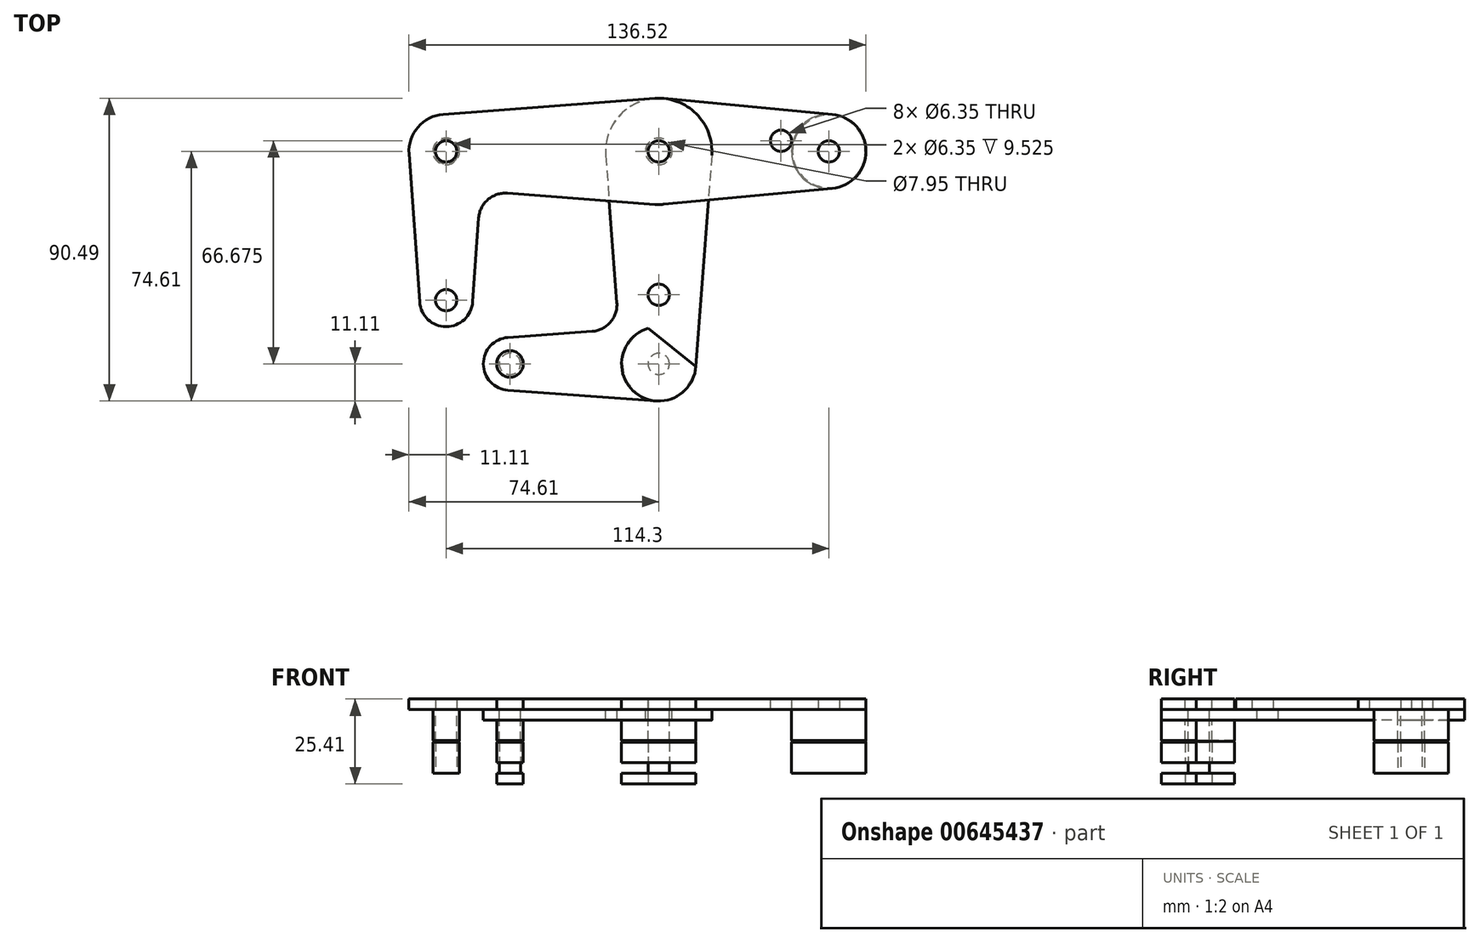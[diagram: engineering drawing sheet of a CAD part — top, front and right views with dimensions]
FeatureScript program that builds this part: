
annotation { "Feature Type Name" : "Feature", "Feature Type Description" : "" }
export const myFeature = defineFeature(function(context is Context, id is Id, definition is map)
    precondition{}
    {
        {
            var Q0;
            Q0=qCreatedBy(makeId("Top.planeOp"),FACE);
            var sketch = newSketch(context, id + "F0", { "sketchPlane" : qUnion([Q0])});
            skCircle(sketch, "E0", {"center": v(0, 0) * mm, "radius": 15.88 * mm});
            skCircle(sketch, "E1", {"center": v(0, 0) * mm, "radius": 3.98 * mm});
            skCircle(sketch, "E2", {"center": v(-63.5, 0) * mm, "radius": 11.11 * mm});
            skCircle(sketch, "E3", {"center": v(50.8, 0) * mm, "radius": 11.11 * mm});
            skCircle(sketch, "E4", {"center": v(-63.5, -44.45) * mm, "radius": 7.94 * mm});
            skCircle(sketch, "E5", {"center": v(50.8, 0) * mm, "radius": 3.18 * mm});
            skCircle(sketch, "E6", {"center": v(36.53, 3.18) * mm, "radius": 3.18 * mm});
            skCircle(sketch, "E7", {"center": v(-63.5, -44.45) * mm, "radius": 3.18 * mm});
            skCircle(sketch, "E8", {"center": v(-63.5, 0) * mm, "radius": 3.18 * mm});
            skLineSegment(sketch, "E9", {"start": v(-71.42, -45.02) * mm, "end": v(-74.58, -0.8) * mm});
            skLineSegment(sketch, "E10", {"start": v(-64.33, 11.08) * mm, "end": v(-1.2, 15.83) * mm});
            skLineSegment(sketch, "E11", {"start": v(1.49, 15.8) * mm, "end": v(51.84, 11.06) * mm});
            skLineSegment(sketch, "E12.MirrorCS", {"start": v(1.49, -15.8) * mm, "end": v(51.84, -11.06) * mm});
            skLineSegment(sketch, "E13.MirrorCS", {"start": v(-45.26, -12.52) * mm, "end": v(-1.2, -15.83) * mm});
            skLineSegment(sketch, "E14", {"start": v(-63.5, 0) * mm, "end": v(-63.5, -44.45) * mm, "construction": true});
            skLineSegment(sketch, "E15.MirrorCS", {"start": v(-55.58, -45.02) * mm, "end": v(-53.78, -19.88) * mm});
            skPoint(sketch, "E16.newPointA", {"position": v(-64.33, -11.08) * mm});
            skPoint(sketch, "E16.newPointB", {"position": v(-52.42, -0.8) * mm});
            skArc(sketch, "E16.filletArc", {"start": v(-45.26, -12.52) * mm, "mid": v(-51.05, -14.43) * mm, "end": v(-53.78, -19.88) * mm});
            skCircle(sketch, "E17", {"center": v(0, 0) * mm, "radius": 3.18 * mm});
            skCircle(sketch, "E18", {"center": v(0, -63.5) * mm, "radius": 11.11 * mm});
            skCircle(sketch, "E19", {"center": v(0, -42.85) * mm, "radius": 3.18 * mm});
            skCircle(sketch, "E20", {"center": v(-44.45, -63.5) * mm, "radius": 7.94 * mm});
            skCircle(sketch, "E21", {"center": v(-44.45, -63.5) * mm, "radius": 3.18 * mm});
            skCircle(sketch, "E22", {"center": v(0, -63.5) * mm, "radius": 3.18 * mm});
            skLineSegment(sketch, "E23", {"start": v(15.83, -1.2) * mm, "end": v(11.08, -64.33) * mm});
            skLineSegment(sketch, "E24", {"start": v(-15.83, -1.2) * mm, "end": v(-12.52, -45.26) * mm});
            skLineSegment(sketch, "E25", {"start": v(-45.02, -71.42) * mm, "end": v(-0.8, -74.58) * mm});
            skLineSegment(sketch, "E26", {"start": v(-45.02, -55.58) * mm, "end": v(-19.88, -53.78) * mm});
            skArc(sketch, "E27.filletArc", {"start": v(-19.88, -53.78) * mm, "mid": v(-14.43, -51.05) * mm, "end": v(-12.52, -45.26) * mm});
            skLineSegment(sketch, "E28", {"start": v(0, -63.5) * mm, "end": v(0, 0) * mm, "construction": true});
            skLineSegment(sketch, "E29", {"start": v(-44.45, -63.5) * mm, "end": v(0, -63.5) * mm, "construction": true});
            skLineSegment(sketch, "E30", {"start": v(0, 0) * mm, "end": v(50.8, 0) * mm, "construction": true});
            skLineSegment(sketch, "E31", {"start": v(-63.5, 0) * mm, "end": v(0, 0) * mm, "construction": true});
            skSolve(sketch);
        }
        {
            var Q0;
            {var subQ0=sQuery(id+"F0.wireOp",EDGE,"E9");Q0=makeQuery(id+"F0.imprint","IMPRINT",FACE,{"disambiguationData":[TD([[makeQuery(id+"F0.imprint","IMPRINT",EDGE,{"derivedFrom":subQ0}),-1.0]])]});}
            var Q1;
            Q1=makeQuery(id+"F0.imprint","IMPRINT",FACE,{"disambiguationData":[TD([[makeQuery(id+"F0.imprint","IMPRINT",EDGE,{"derivedFrom":sQuery(id+"F0.wireOp",EDGE,"E1")}),-1.0]])]});
            var Q2;
            Q2=makeQuery(id+"F0.imprint","IMPRINT",FACE,{"disambiguationData":[TD([[makeQuery(id+"F0.imprint","IMPRINT",EDGE,{"derivedFrom":sQuery(id+"F0.wireOp",EDGE,"E6")}),-1.0]])]});
            var Q3;
            Q3=makeQuery(id+"F0.imprint","IMPRINT",FACE,{"disambiguationData":[TD([[makeQuery(id+"F0.imprint","IMPRINT",EDGE,{"derivedFrom":sQuery(id+"F0.wireOp",EDGE,"E5")}),-1.0]])]});
            var Q4;
            Q4=makeQuery(id+"F0.imprint","IMPRINT",FACE,{"disambiguationData":[TD([[makeQuery(id+"F0.imprint","IMPRINT",EDGE,{"derivedFrom":sQuery(id+"F0.wireOp",EDGE,"E8")}),-1.0]])]});
            var Q5;
            Q5=makeQuery(id+"F0.imprint","IMPRINT",FACE,{"disambiguationData":[TD([[makeQuery(id+"F0.imprint","IMPRINT",EDGE,{"derivedFrom":sQuery(id+"F0.wireOp",EDGE,"E7")}),-1.0]])]});
            var Q6;
            {var subQ0=sQuery(id+"F0.wireOp",EDGE,"E13.MirrorCS");var subQ1=sQuery(id+"F0.wireOp",EDGE,"E0");var subQ2=makeQuery(id+"F0.imprint","INTERSECT",VERTEX,{"derivedFrom":[subQ1,subQ0]});Q6=makeQuery(id+"F0.imprint","IMPRINT",FACE,{"disambiguationData":[TD([[makeQuery(id+"F0.imprint","IMPRINT",EDGE,{"disambiguationData":[TD([[subQ2,1.0]])],"derivedFrom":subQ1}),-1.0]])]});}
            var Q7;
            {var subQ0=sQuery(id+"F0.wireOp",EDGE,"E12.MirrorCS");var subQ1=sQuery(id+"F0.wireOp",EDGE,"E0");var subQ2=makeQuery(id+"F0.imprint","INTERSECT",VERTEX,{"derivedFrom":[subQ1,subQ0]});Q7=makeQuery(id+"F0.imprint","IMPRINT",FACE,{"disambiguationData":[TD([[makeQuery(id+"F0.imprint","IMPRINT",EDGE,{"disambiguationData":[TD([[subQ2,-1.0]])],"derivedFrom":subQ1}),-1.0]])]});}
            var Q8;
            Q8=makeQuery(id+"F0.imprint","IMPRINT",FACE,{"disambiguationData":[TD([[makeQuery(id+"F0.imprint","IMPRINT",EDGE,{"derivedFrom":sQuery(id+"F0.wireOp",EDGE,"E1")}),1.0]])]});
            extrude(context, id + "F1", {"entities" : qUnion([Q0, Q1, Q2, Q3, Q4, Q5, Q6, Q7, Q8]), "depth" : 3.17 * mm, "offsetDistance" : 25.4 * mm});
        }
        {
            var Q0;
            Q0=makeQuery(id+"F0.imprint","IMPRINT",FACE,{"disambiguationData":[TD([[makeQuery(id+"F0.imprint","IMPRINT",EDGE,{"derivedFrom":sQuery(id+"F0.wireOp",EDGE,"E1")}),-1.0]])]});
            var Q1;
            {var subQ0=sQuery(id+"F0.wireOp",EDGE,"E13.MirrorCS");var subQ1=sQuery(id+"F0.wireOp",EDGE,"E0");var subQ2=makeQuery(id+"F0.imprint","INTERSECT",VERTEX,{"derivedFrom":[subQ1,subQ0]});Q1=makeQuery(id+"F0.imprint","IMPRINT",FACE,{"disambiguationData":[TD([[makeQuery(id+"F0.imprint","IMPRINT",EDGE,{"disambiguationData":[TD([[subQ2,1.0]])],"derivedFrom":subQ1}),-1.0]])]});}
            var Q2;
            {var subQ0=sQuery(id+"F0.wireOp",EDGE,"E12.MirrorCS");var subQ1=sQuery(id+"F0.wireOp",EDGE,"E0");var subQ2=makeQuery(id+"F0.imprint","INTERSECT",VERTEX,{"derivedFrom":[subQ1,subQ0]});Q2=makeQuery(id+"F0.imprint","IMPRINT",FACE,{"disambiguationData":[TD([[makeQuery(id+"F0.imprint","IMPRINT",EDGE,{"disambiguationData":[TD([[subQ2,-1.0]])],"derivedFrom":subQ1}),-1.0]])]});}
            var Q3;
            Q3=makeQuery(id+"F0.imprint","IMPRINT",FACE,{"disambiguationData":[TD([[makeQuery(id+"F0.imprint","IMPRINT",EDGE,{"derivedFrom":sQuery(id+"F0.wireOp",EDGE,"E19")}),-1.0]])]});
            var Q4;
            Q4=makeQuery(id+"F0.imprint","IMPRINT",FACE,{"disambiguationData":[TD([[makeQuery(id+"F0.imprint","IMPRINT",EDGE,{"derivedFrom":sQuery(id+"F0.wireOp",EDGE,"E22")}),-1.0]])]});
            var Q5;
            Q5=makeQuery(id+"F0.imprint","IMPRINT",FACE,{"disambiguationData":[TD([[makeQuery(id+"F0.imprint","IMPRINT",EDGE,{"derivedFrom":sQuery(id+"F0.wireOp",EDGE,"E21")}),-1.0]])]});
            extrude(context, id + "F2", {"entities" : qUnion([Q0, Q1, Q2, Q3, Q4, Q5]), "oppositeDirection" : true, "depth" : 3.17 * mm, "offsetDistance" : 25.4 * mm});
        }
        {
            var Q0;
            Q0=makeQuery(id+"F1.opExtrude","CAP_FACE",FACE,{"disambiguationData":[OSD([sQuery(id+"F0.wireOp",EDGE,"E0"),sQuery(id+"F0.wireOp",EDGE,"E2"),sQuery(id+"F0.wireOp",EDGE,"E3"),sQuery(id+"F0.wireOp",EDGE,"E4"),sQuery(id+"F0.wireOp",EDGE,"E5"),sQuery(id+"F0.wireOp",EDGE,"E6"),sQuery(id+"F0.wireOp",EDGE,"E7"),sQuery(id+"F0.wireOp",EDGE,"E8"),sQuery(id+"F0.wireOp",EDGE,"E9"),sQuery(id+"F0.wireOp",EDGE,"E10"),sQuery(id+"F0.wireOp",EDGE,"E11"),sQuery(id+"F0.wireOp",EDGE,"E12.MirrorCS"),sQuery(id+"F0.wireOp",EDGE,"E13.MirrorCS"),sQuery(id+"F0.wireOp",EDGE,"E15.MirrorCS"),sQuery(id+"F0.wireOp",EDGE,"E16.filletArc"),sQuery(id+"F0.wireOp",EDGE,"E17")])],"isStart":false});
            var sketch = newSketch(context, id + "F3", { "sketchPlane" : qUnion([Q0])});
            skCircle(sketch, "E32", {"center": v(0, -63.5) * mm, "radius": 11.11 * mm});
            skLineSegment(sketch, "E33", {"start": v(-3.15, -52.84) * mm, "end": v(11.09, -64.24) * mm});
            skLineSegment(sketch, "E34", {"start": v(3.97, -58.54) * mm, "end": v(50.8, 0) * mm, "construction": true});
            skCircle(sketch, "E35", {"center": v(-63.5, 0) * mm, "radius": 3.98 * mm});
            skCircle(sketch, "E36", {"center": v(0, 0) * mm, "radius": 3.98 * mm});
            skCircle(sketch, "E37", {"center": v(50.8, 0) * mm, "radius": 11.11 * mm});
            skCircle(sketch, "E38", {"center": v(-44.45, -63.5) * mm, "radius": 3.98 * mm});
            skSolve(sketch);
        }
        {
            var Q0;
            Q0=qCreatedBy(makeId("Top.planeOp"),FACE);
            cPlane(context, id + "F4", {"entities" : qUnion([Q0]), "cplaneType" : CPlaneType.OFFSET, "offset" : 9.52 * mm, "oppositeDirection" : true, "width" : 152.4 * mm, "height" : 152.4 * mm});
        }
        {
            var Q0;
            Q0=makeQuery(id+"F0.imprint","IMPRINT",FACE,{"disambiguationData":[TD([[makeQuery(id+"F0.imprint","IMPRINT",EDGE,{"derivedFrom":sQuery(id+"F0.wireOp",EDGE,"E22")}),1.0]])]});
            var Q1;
            {var subQ2=sQuery(id+"F3.wireOp",EDGE,"E33");Q1=makeQuery(id+"F3.imprint","IMPRINT",FACE,{"disambiguationData":[TD([[makeQuery(id+"F3.imprint","IMPRINT",EDGE,{"derivedFrom":subQ2}),-1.0]])]});}
            var Q2;
            Q2=makeQuery(id+"F0.imprint","IMPRINT",FACE,{"disambiguationData":[TD([[makeQuery(id+"F0.imprint","IMPRINT",EDGE,{"derivedFrom":sQuery(id+"F0.wireOp",EDGE,"E21")}),1.0]])]});
            var Q3;
            Q3=makeQuery(id+"F3.imprint","IMPRINT",FACE,{"disambiguationData":[TD([[makeQuery(id+"F3.imprint","IMPRINT",EDGE,{"derivedFrom":sQuery(id+"F3.wireOp",EDGE,"E38")}),1.0]])]});
            var Q4;
            Q4=makeQuery(id+"F0.imprint","IMPRINT",FACE,{"disambiguationData":[TD([[makeQuery(id+"F0.imprint","IMPRINT",EDGE,{"derivedFrom":sQuery(id+"F0.wireOp",EDGE,"E8")}),1.0]])]});
            var Q5;
            Q5=makeQuery(id+"F3.imprint","IMPRINT",FACE,{"disambiguationData":[TD([[makeQuery(id+"F3.imprint","IMPRINT",EDGE,{"derivedFrom":sQuery(id+"F3.wireOp",EDGE,"E35")}),1.0]])]});
            var Q6;
            Q6=makeQuery(id+"F0.imprint","IMPRINT",FACE,{"disambiguationData":[TD([[makeQuery(id+"F0.imprint","IMPRINT",EDGE,{"derivedFrom":sQuery(id+"F0.wireOp",EDGE,"E5")}),1.0]])]});
            var Q7;
            Q7=makeQuery(id+"F0.imprint","IMPRINT",FACE,{"disambiguationData":[TD([[makeQuery(id+"F0.imprint","IMPRINT",EDGE,{"derivedFrom":sQuery(id+"F0.wireOp",EDGE,"E5")}),-1.0]])]});
            var Q8;
            Q8=qCreatedBy(id+"F4.planeOp",FACE);
            extrude(context, id + "F5", {"entities" : qUnion([Q0, Q1, Q2, Q3, Q4, Q5, Q6, Q7]), "endBound" : BoundingType.UP_TO_SURFACE, "oppositeDirection" : true, "depth" : 25.4 * mm, "endBoundEntityFace" : qUnion([Q8]), "offsetDistance" : 25.4 * mm});
        }
        {
            var Q0;
            Q0=makeQuery(id+"F1.opExtrude","SWEPT_BODY",BODY,{"disambiguationData":[OSD([sQuery(id+"F0.wireOp",EDGE,"E0"),sQuery(id+"F0.wireOp",EDGE,"E2"),sQuery(id+"F0.wireOp",EDGE,"E3"),sQuery(id+"F0.wireOp",EDGE,"E4"),sQuery(id+"F0.wireOp",EDGE,"E5"),sQuery(id+"F0.wireOp",EDGE,"E6"),sQuery(id+"F0.wireOp",EDGE,"E7"),sQuery(id+"F0.wireOp",EDGE,"E8"),sQuery(id+"F0.wireOp",EDGE,"E9"),sQuery(id+"F0.wireOp",EDGE,"E10"),sQuery(id+"F0.wireOp",EDGE,"E11"),sQuery(id+"F0.wireOp",EDGE,"E12.MirrorCS"),sQuery(id+"F0.wireOp",EDGE,"E13.MirrorCS"),sQuery(id+"F0.wireOp",EDGE,"E15.MirrorCS"),sQuery(id+"F0.wireOp",EDGE,"E16.filletArc"),sQuery(id+"F0.wireOp",EDGE,"E17")])]});
            var Q1;
            Q1=makeQuery(id+"F2.opExtrude","SWEPT_BODY",BODY,{"disambiguationData":[OSD([sQuery(id+"F0.wireOp",EDGE,"E0"),sQuery(id+"F0.wireOp",EDGE,"E1"),sQuery(id+"F0.wireOp",EDGE,"E18"),sQuery(id+"F0.wireOp",EDGE,"E19"),sQuery(id+"F0.wireOp",EDGE,"E20"),sQuery(id+"F0.wireOp",EDGE,"E21"),sQuery(id+"F0.wireOp",EDGE,"E22"),sQuery(id+"F0.wireOp",EDGE,"E23"),sQuery(id+"F0.wireOp",EDGE,"E24"),sQuery(id+"F0.wireOp",EDGE,"E25"),sQuery(id+"F0.wireOp",EDGE,"E26"),sQuery(id+"F0.wireOp",EDGE,"E27.filletArc")])]});
            var Q2;
            Q2=makeQuery(id+"F5.opExtrude","SWEPT_BODY",BODY,{"disambiguationData":[OSD([sQuery(id+"F0.wireOp",EDGE,"E8")])]});
            var Q3;
            Q3=makeQuery(id+"F5.opExtrude","SWEPT_BODY",BODY,{"disambiguationData":[OSD([sQuery(id+"F0.wireOp",EDGE,"E8"),sQuery(id+"F3.wireOp",EDGE,"E35")])]});
            var Q4;
            Q4=makeQuery(id+"F5.opExtrude","SWEPT_BODY",BODY,{"disambiguationData":[OSD([sQuery(id+"F0.wireOp",EDGE,"E21")])]});
            var Q5;
            Q5=makeQuery(id+"F5.opExtrude","SWEPT_BODY",BODY,{"disambiguationData":[OSD([sQuery(id+"F3.wireOp",EDGE,"E38")])]});
            var Q6;
            Q6=makeQuery(id+"F5.opExtrude","SWEPT_BODY",BODY,{"disambiguationData":[OSD([sQuery(id+"F0.wireOp",EDGE,"E22")])]});
            var Q7;
            Q7=makeQuery(id+"F5.opExtrude","SWEPT_BODY",BODY,{"disambiguationData":[OSD([sQuery(id+"F3.wireOp",EDGE,"E32"),sQuery(id+"F3.wireOp",EDGE,"E33")])]});
            var Q8;
            Q8=makeQuery(id+"F5.opExtrude","SWEPT_BODY",BODY,{"disambiguationData":[OSD([sQuery(id+"F0.wireOp",EDGE,"E3")])]});
            booleanBodies(context, id + "F6", {"operationType" : BooleanOperationType.SUBTRACTION, "tools" : qUnion([Q0, Q1]), "targets" : qUnion([Q2, Q3, Q4, Q5, Q6, Q7, Q8]), "keepTools" : true});
        }
        {
            var Q0;
            Q0=makeQuery(id+"F5.opExtrude","CAP_EDGE",EDGE,{"disambiguationData":[OSD([sQuery(id+"F3.wireOp",EDGE,"E35")])],"isStart":false});
            var Q1;
            Q1=makeQuery(id+"F5.opExtrude","CAP_EDGE",EDGE,{"disambiguationData":[OSD([sQuery(id+"F3.wireOp",EDGE,"E38")])],"isStart":false});
            var Q2;
            Q2=makeQuery(id+"F5.opExtrude","CAP_EDGE",EDGE,{"disambiguationData":[OSD([sQuery(id+"F3.wireOp",EDGE,"E32")])],"isStart":false});
            var Q3;
            Q3=makeQuery(id+"F5.opExtrude","CAP_EDGE",EDGE,{"disambiguationData":[OSD([sQuery(id+"F0.wireOp",EDGE,"E3")])],"isStart":false});
            chamfer(context, id + "F7", {"entities" : qUnion([Q0, Q1, Q2, Q3]), "width" : 0.25 * mm, "tangentPropagation" : true});
        }
        {
            var Q0;
            Q0=makeQuery(id+"F5.opExtrude","SWEPT_BODY",BODY,{"disambiguationData":[OSD([sQuery(id+"F0.wireOp",EDGE,"E8"),sQuery(id+"F3.wireOp",EDGE,"E35")])]});
            var Q1;
            Q1=makeQuery(id+"F5.opExtrude","SWEPT_BODY",BODY,{"disambiguationData":[OSD([sQuery(id+"F0.wireOp",EDGE,"E8")])]});
            var Q2;
            Q2=makeQuery(id+"F5.opExtrude","SWEPT_BODY",BODY,{"disambiguationData":[OSD([sQuery(id+"F3.wireOp",EDGE,"E38")])]});
            var Q3;
            Q3=makeQuery(id+"F5.opExtrude","SWEPT_BODY",BODY,{"disambiguationData":[OSD([sQuery(id+"F0.wireOp",EDGE,"E21")])]});
            var Q4;
            Q4=makeQuery(id+"F5.opExtrude","SWEPT_BODY",BODY,{"disambiguationData":[OSD([sQuery(id+"F3.wireOp",EDGE,"E32"),sQuery(id+"F3.wireOp",EDGE,"E33")])]});
            var Q5;
            Q5=makeQuery(id+"F5.opExtrude","SWEPT_BODY",BODY,{"disambiguationData":[OSD([sQuery(id+"F0.wireOp",EDGE,"E22")])]});
            var Q6;
            Q6=makeQuery(id+"F5.opExtrude","SWEPT_BODY",BODY,{"disambiguationData":[OSD([sQuery(id+"F0.wireOp",EDGE,"E3")])]});
            var Q7;
            Q7=qCreatedBy(id+"F4.planeOp",FACE);
            mirror(context, id + "F8", {"entities" : qUnion([Q0, Q1, Q2, Q3, Q4, Q5, Q6]), "mirrorPlane" : qUnion([Q7])});
        }
    });
